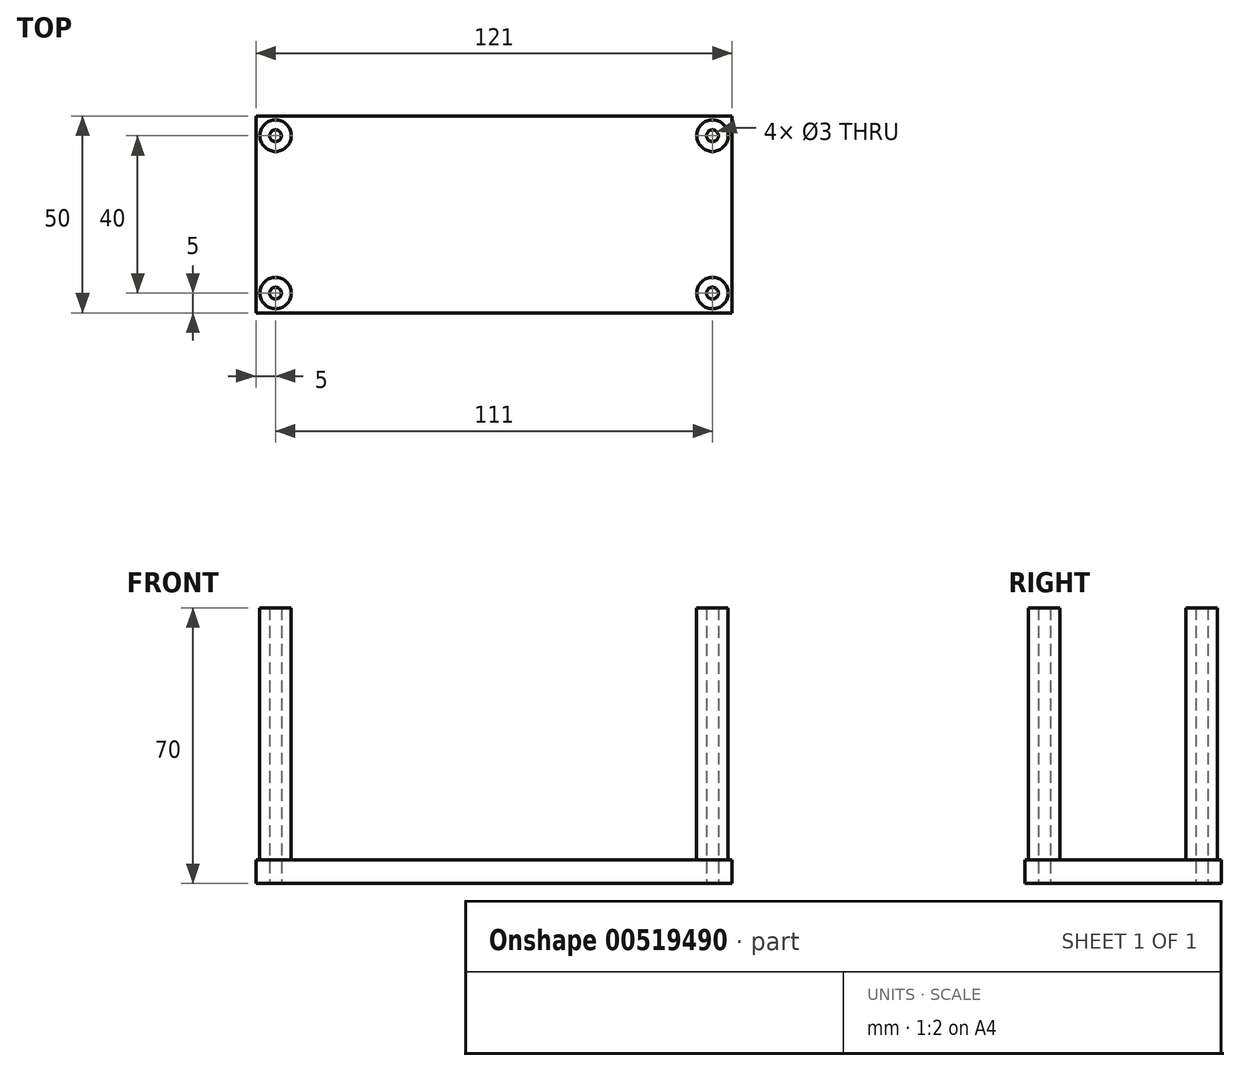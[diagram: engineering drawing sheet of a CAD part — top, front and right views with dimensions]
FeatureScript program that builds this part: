
annotation { "Feature Type Name" : "Feature", "Feature Type Description" : "" }
export const myFeature = defineFeature(function(context is Context, id is Id, definition is map)
    precondition{}
    {
        {
            var Q0;
            Q0=qCreatedBy(makeId("Top.planeOp"),FACE);
            var sketch = newSketch(context, id + "F0", { "sketchPlane" : qUnion([Q0])});
            skLineSegment(sketch, "E0.bottom", {"start": v(60.5, 25) * mm, "end": v(-60.5, 25) * mm});
            skLineSegment(sketch, "E0.top", {"start": v(60.5, -25) * mm, "end": v(-60.5, -25) * mm});
            skLineSegment(sketch, "E0.left", {"start": v(60.5, 25) * mm, "end": v(60.5, -25) * mm});
            skLineSegment(sketch, "E0.right", {"start": v(-60.5, 25) * mm, "end": v(-60.5, -25) * mm});
            skPoint(sketch, "E0.middle", {"position": v(0, 0) * mm});
            skLineSegment(sketch, "E1.bottom", {"start": v(50.5, 15) * mm, "end": v(-50.5, 15) * mm});
            skLineSegment(sketch, "E1.top", {"start": v(50.5, -15) * mm, "end": v(-50.5, -15) * mm});
            skLineSegment(sketch, "E1.left", {"start": v(50.5, 15) * mm, "end": v(50.5, -15) * mm});
            skLineSegment(sketch, "E1.right", {"start": v(-50.5, 15) * mm, "end": v(-50.5, -15) * mm});
            skPoint(sketch, "E2", {"position": v(-55.5, 20) * mm});
            skPoint(sketch, "E3", {"position": v(55.5, 20) * mm});
            skPoint(sketch, "E4", {"position": v(55.5, -20) * mm});
            skPoint(sketch, "E5", {"position": v(-55.5, -20) * mm});
            skCircle(sketch, "E6", {"center": v(-55.5, 20) * mm, "radius": 4 * mm});
            skCircle(sketch, "E7", {"center": v(-55.5, 20) * mm, "radius": 1.5 * mm});
            skCircle(sketch, "E8", {"center": v(55.5, 20) * mm, "radius": 4 * mm});
            skCircle(sketch, "E9", {"center": v(55.5, 20) * mm, "radius": 1.5 * mm});
            skCircle(sketch, "E10", {"center": v(55.5, -20) * mm, "radius": 4 * mm});
            skCircle(sketch, "E11", {"center": v(55.5, -20) * mm, "radius": 1.5 * mm});
            skCircle(sketch, "E12", {"center": v(-55.5, -20) * mm, "radius": 4 * mm});
            skCircle(sketch, "E13", {"center": v(-55.5, -20) * mm, "radius": 1.5 * mm});
            skSolve(sketch);
        }
        {
            var Q0;
            Q0=makeQuery(id+"F0.imprint","IMPRINT",FACE,{"disambiguationData":[TD([[makeQuery(id+"F0.imprint","IMPRINT",EDGE,{"derivedFrom":sQuery(id+"F0.wireOp",EDGE,"E0.bottom")}),1.0]])]});
            var Q1;
            Q1=makeQuery(id+"F0.imprint","IMPRINT",FACE,{"disambiguationData":[TD([[makeQuery(id+"F0.imprint","IMPRINT",EDGE,{"derivedFrom":sQuery(id+"F0.wireOp",EDGE,"E1.bottom")}),1.0]])]});
            extrude(context, id + "F1", {"entities" : qUnion([Q0, Q1]), "depth" : 6 * mm, "offsetDistance" : 25 * mm});
        }
        {
            var Q0;
            Q0=makeQuery(id+"F0.imprint","IMPRINT",FACE,{"disambiguationData":[TD([[makeQuery(id+"F0.imprint","IMPRINT",EDGE,{"derivedFrom":sQuery(id+"F0.wireOp",EDGE,"E6")}),1.0]])]});
            var Q1;
            Q1=makeQuery(id+"F0.imprint","IMPRINT",FACE,{"disambiguationData":[TD([[makeQuery(id+"F0.imprint","IMPRINT",EDGE,{"derivedFrom":sQuery(id+"F0.wireOp",EDGE,"E8")}),1.0]])]});
            var Q2;
            Q2=makeQuery(id+"F0.imprint","IMPRINT",FACE,{"disambiguationData":[TD([[makeQuery(id+"F0.imprint","IMPRINT",EDGE,{"derivedFrom":sQuery(id+"F0.wireOp",EDGE,"E10")}),1.0]])]});
            var Q3;
            Q3=makeQuery(id+"F0.imprint","IMPRINT",FACE,{"disambiguationData":[TD([[makeQuery(id+"F0.imprint","IMPRINT",EDGE,{"derivedFrom":sQuery(id+"F0.wireOp",EDGE,"E12")}),1.0]])]});
            extrude(context, id + "F2", {"entities" : qUnion([Q0, Q1, Q2, Q3]), "operationType" : NewBodyOperationType.ADD, "depth" : 70 * mm, "offsetDistance" : 25 * mm});
        }
    });
